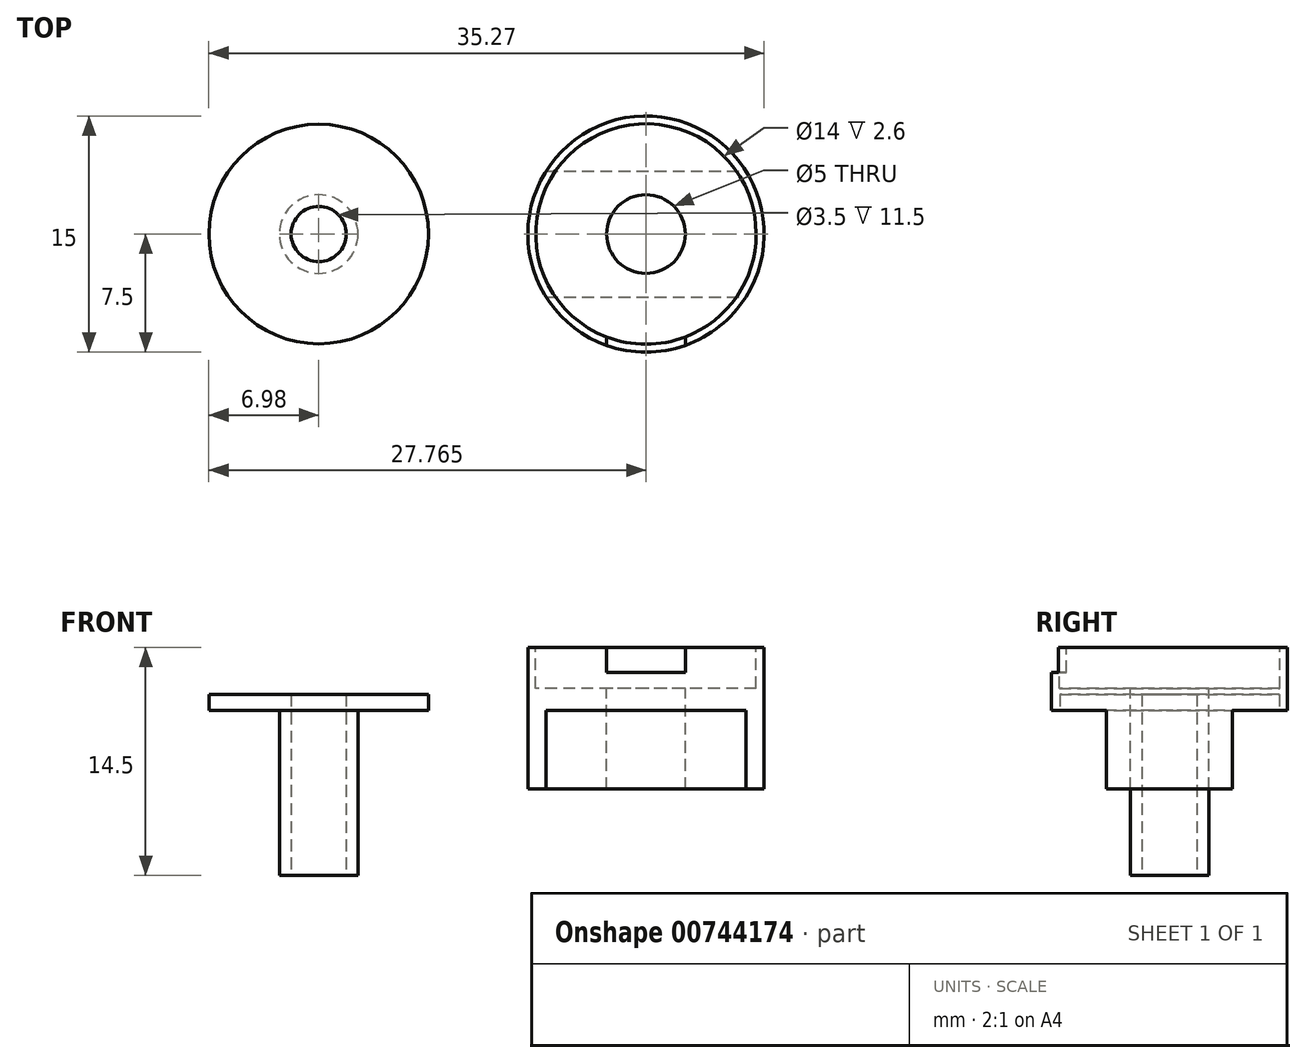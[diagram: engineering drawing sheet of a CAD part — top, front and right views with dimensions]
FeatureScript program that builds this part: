
annotation { "Feature Type Name" : "Feature", "Feature Type Description" : "" }
export const myFeature = defineFeature(function(context is Context, id is Id, definition is map)
    precondition{}
    {
        {
            var Q0;
            Q0=qCreatedBy(makeId("Top.planeOp"),FACE);
            var sketch = newSketch(context, id + "F0", { "sketchPlane" : qUnion([Q0])});
            skCircle(sketch, "E0", {"center": v(0, 0) * mm, "radius": 1.75 * mm});
            skCircle(sketch, "E1", {"center": v(0, 0) * mm, "radius": 6.97 * mm});
            skCircle(sketch, "E2", {"center": v(0, 0) * mm, "radius": 2.5 * mm});
            skSolve(sketch);
        }
        {
            var Q0;
            Q0=makeQuery(id+"F0.imprint","IMPRINT",FACE,{"disambiguationData":[TD([[makeQuery(id+"F0.imprint","IMPRINT",EDGE,{"derivedFrom":sQuery(id+"F0.wireOp",EDGE,"E0")}),-1.0]])]});
            var Q1;
            Q1=makeQuery(id+"F0.imprint","IMPRINT",FACE,{"disambiguationData":[TD([[makeQuery(id+"F0.imprint","IMPRINT",EDGE,{"derivedFrom":sQuery(id+"F0.wireOp",EDGE,"E1")}),1.0]])]});
            var Q2;
            Q2=sQuery(id+"F0.wireOp",EDGE,"E1");
            extrude(context, id + "F1", {"entities" : qUnion([Q0, Q1]), "surfaceEntities" : qUnion([Q2]), "depth" : 1 * mm, "offsetDistance" : 25 * mm});
        }
        {
            var Q0;
            Q0=makeQuery(id+"F0.imprint","IMPRINT",FACE,{"disambiguationData":[TD([[makeQuery(id+"F0.imprint","IMPRINT",EDGE,{"derivedFrom":sQuery(id+"F0.wireOp",EDGE,"E0")}),-1.0]])]});
            var Q1;
            Q1=sQuery(id+"F0.wireOp",EDGE,"E2");
            extrude(context, id + "F2", {"entities" : qUnion([Q0]), "operationType" : NewBodyOperationType.ADD, "surfaceEntities" : qUnion([Q1]), "oppositeDirection" : true, "depth" : 10.5 * mm, "offsetDistance" : 25 * mm});
        }
        {
            var Q0;
            Q0=qCreatedBy(makeId("Front.planeOp"),FACE);
            var sketch = newSketch(context, id + "F3", { "sketchPlane" : qUnion([Q0])});
            skLineSegment(sketch, "E3", {"start": v(28.29, 4) * mm, "end": v(27.79, 4) * mm});
            skLineSegment(sketch, "E4", {"start": v(27.79, 4) * mm, "end": v(27.79, 1.4) * mm});
            skLineSegment(sketch, "E5", {"start": v(27.79, 1.4) * mm, "end": v(23.29, 1.4) * mm});
            skLineSegment(sketch, "E6", {"start": v(23.29, 1.4) * mm, "end": v(23.29, -5) * mm});
            skLineSegment(sketch, "E7", {"start": v(20.79, 5.18) * mm, "end": v(20.79, -6.53) * mm, "construction": true});
            skLineSegment(sketch, "E8", {"start": v(28.29, 4) * mm, "end": v(28.29, -5) * mm});
            skLineSegment(sketch, "E9", {"start": v(23.29, -5) * mm, "end": v(28.29, -5) * mm});
            skSolve(sketch);
        }
        {
            var Q0;
            Q0=makeQuery(id+"F3.imprint","IMPRINT",FACE,{"disambiguationData":[TD([[makeQuery(id+"F3.imprint","IMPRINT",EDGE,{"derivedFrom":sQuery(id+"F3.wireOp",EDGE,"AlYA6rKq-fiig-BBCV-Xiqp-ft7WZwbce5R2")}),1.0]])]});
            var Q1;
            Q1=makeQuery(id+"F3.imprint","IMPRINT",FACE,{"disambiguationData":[TD([[makeQuery(id+"F3.imprint","IMPRINT",EDGE,{"derivedFrom":sQuery(id+"F3.wireOp",EDGE,"E3")}),1.0]])]});
            var Q2;
            Q2=sQuery(id+"F3.wireOp",EDGE,"chtU6L97-KUWa-k6fX-va27-cWDTODDnlhp8");
            var Q3;
            Q3=sQuery(id+"F3.wireOp",EDGE,"AlYA6rKq-fiig-BBCV-Xiqp-ft7WZwbce5R2");
            var Q4;
            Q4=sQuery(id+"F3.wireOp",EDGE,"E5");
            var Q5;
            Q5=sQuery(id+"F3.wireOp",EDGE,"E4");
            var Q6;
            Q6=sQuery(id+"F3.wireOp",EDGE,"EKweZBcX-0bdW-dXhE-Aki5-89H8m73LfTbS");
            var Q7;
            Q7=sQuery(id+"F3.wireOp",EDGE,"ZGMUXvWB-WUbi-oums-hqUC-sTKsELbzMWuZ");
            var Q8;
            Q8=sQuery(id+"F3.wireOp",EDGE,"E6");
            var Q9;
            Q9=sQuery(id+"F3.wireOp",EDGE,"XAqISl7f-3O0B-Lr7O-hAjR-8VHck1D6WNRk");
            var Q10;
            Q10=sQuery(id+"F3.wireOp",EDGE,"PQDrq51b-85sZ-VkBi-vOIX-TeJFj0cnGDnC");
            var Q11;
            Q11=sQuery(id+"F3.wireOp",EDGE,"E3");
            var Q12;
            Q12=sQuery(id+"F3.wireOp",EDGE,"4IBXs6gY-Wsi9-MYEh-jOon-pm4EWKZcu0Ms");
            var Q13;
            Q13=sQuery(id+"F3.wireOp",EDGE,"E7");
            revolve(context, id + "F4", {"surfaceOperationType" : NewSurfaceOperationType.NEW, "entities" : qUnion([Q0, Q1]), "surfaceEntities" : qUnion([Q2, Q3, Q4, Q5, Q6, Q7, Q8, Q9, Q10, Q11, Q12]), "axis" : qUnion([Q13]), "revolveType" : RevolveType.FULL});
        }
        {
            var Q0;
            Q0=qCreatedBy(makeId("Front.planeOp"),FACE);
            var sketch = newSketch(context, id + "F5", { "sketchPlane" : qUnion([Q0])});
            skLineSegment(sketch, "E10.top", {"start": v(18.29, 2.4) * mm, "end": v(23.29, 2.4) * mm});
            skLineSegment(sketch, "E10.left", {"start": v(18.29, 4) * mm, "end": v(18.29, 2.4) * mm});
            skLineSegment(sketch, "E10.right", {"start": v(23.29, 4) * mm, "end": v(23.29, 2.4) * mm});
            skLineSegment(sketch, "E11", {"start": v(18.29, 4) * mm, "end": v(23.29, 4) * mm});
            skSolve(sketch);
        }
        {
            var Q0;
            Q0=makeQuery(id+"F5.imprint","IMPRINT",FACE,{"disambiguationData":[TD([[makeQuery(id+"F5.imprint","IMPRINT",EDGE,{"derivedFrom":sQuery(id+"F5.wireOp",EDGE,"E10.top")}),1.0]])]});
            var Q1;
            Q1=sQuery(id+"F5.wireOp",EDGE,"E10.right");
            var Q2;
            Q2=sQuery(id+"F5.wireOp",EDGE,"E11");
            var Q3;
            Q3=sQuery(id+"F5.wireOp",EDGE,"E10.left");
            var Q4;
            Q4=sQuery(id+"F5.wireOp",EDGE,"E10.top");
            extrude(context, id + "F6", {"entities" : qUnion([Q0]), "operationType" : NewBodyOperationType.REMOVE, "surfaceEntities" : qUnion([Q1, Q2, Q3, Q4]), "endBound" : BoundingType.THROUGH_ALL, "depth" : 25 * mm, "offsetDistance" : 25 * mm});
        }
        {
            var Q0;
            Q0=makeQuery(id+"F4.opRevolve","SWEPT_FACE",FACE,{"disambiguationData":[OSD([sQuery(id+"F3.wireOp",EDGE,"E9")])]});
            var sketch = newSketch(context, id + "F7", { "sketchPlane" : qUnion([Q0])});
            skLineSegment(sketch, "E12.bottom", {"start": v(13.29, 4) * mm, "end": v(28.29, 4) * mm});
            skLineSegment(sketch, "E12.top", {"start": v(13.29, -4) * mm, "end": v(28.29, -4) * mm});
            skLineSegment(sketch, "E12.left", {"start": v(13.29, 4) * mm, "end": v(13.29, -4) * mm});
            skLineSegment(sketch, "E12.right", {"start": v(28.29, 4) * mm, "end": v(28.29, -4) * mm});
            skSolve(sketch);
        }
        {
            var Q0;
            {var subQ0=sQuery(id+"F7.wireOp",EDGE,"E12.bottom");var subQ1=makeQuery(id+"F4.opRevolve","SWEPT_EDGE",EDGE,{"disambiguationData":[OSD([sQuery(id+"F3.wireOp",EDGE,"E8"),sQuery(id+"F3.wireOp",EDGE,"E9")])]});var subQ2=makeQuery(id+"F7.imprint","INTERSECT",VERTEX,{"disambiguationData":[OD(0.0)],"derivedFrom":[subQ1,subQ0]});Q0=makeQuery(id+"F7.imprint","IMPRINT",FACE,{"disambiguationData":[TD([[makeQuery(id+"F7.imprint","IMPRINT",EDGE,{"disambiguationData":[TD([[subQ2,-1.0]])],"derivedFrom":subQ0}),1.0]])]});}
            var Q1;
            {var subQ0=sQuery(id+"F7.wireOp",EDGE,"E12.top");var subQ1=makeQuery(id+"F4.opRevolve","SWEPT_EDGE",EDGE,{"disambiguationData":[OSD([sQuery(id+"F3.wireOp",EDGE,"E8"),sQuery(id+"F3.wireOp",EDGE,"E9")])]});var subQ2=makeQuery(id+"F7.imprint","INTERSECT",VERTEX,{"disambiguationData":[OD(0.0)],"derivedFrom":[subQ1,subQ0]});Q1=makeQuery(id+"F7.imprint","IMPRINT",FACE,{"disambiguationData":[TD([[makeQuery(id+"F7.imprint","IMPRINT",EDGE,{"disambiguationData":[TD([[subQ2,-1.0]])],"derivedFrom":subQ0}),-1.0]])]});}
            extrude(context, id + "F8", {"entities" : qUnion([Q0, Q1]), "operationType" : NewBodyOperationType.REMOVE, "oppositeDirection" : true, "depth" : 5 * mm, "offsetDistance" : 25 * mm});
        }
    });
